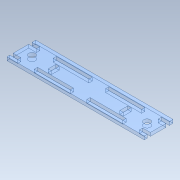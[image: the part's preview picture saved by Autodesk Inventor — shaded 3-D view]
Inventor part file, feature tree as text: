
AUTODESK INVENTOR PART (.ipt)
format: ipt  version: 2022 (Build 260153000, 153)  size: 329,216 bytes
history: native  units: mm
features: extrude x1, sketch x1
ambient origin geometry x8: Origin, YZ Plane, XZ Plane, XY Plane, X Axis, Y Axis, Z Axis, Center Point
bodies: Body1 (feature_tree)
feature tree (2):
  extrude  "Extrusion2"  [1 undecoded]
  sketch  "Sketch2"  dims[d3=3.0mm d4=0.0mm]
note: 1 required parameter value undecoded (feature->parameter linkage not recoverable at this tier; creation-order binding heuristic only, values carry confidence <= 0.55)
